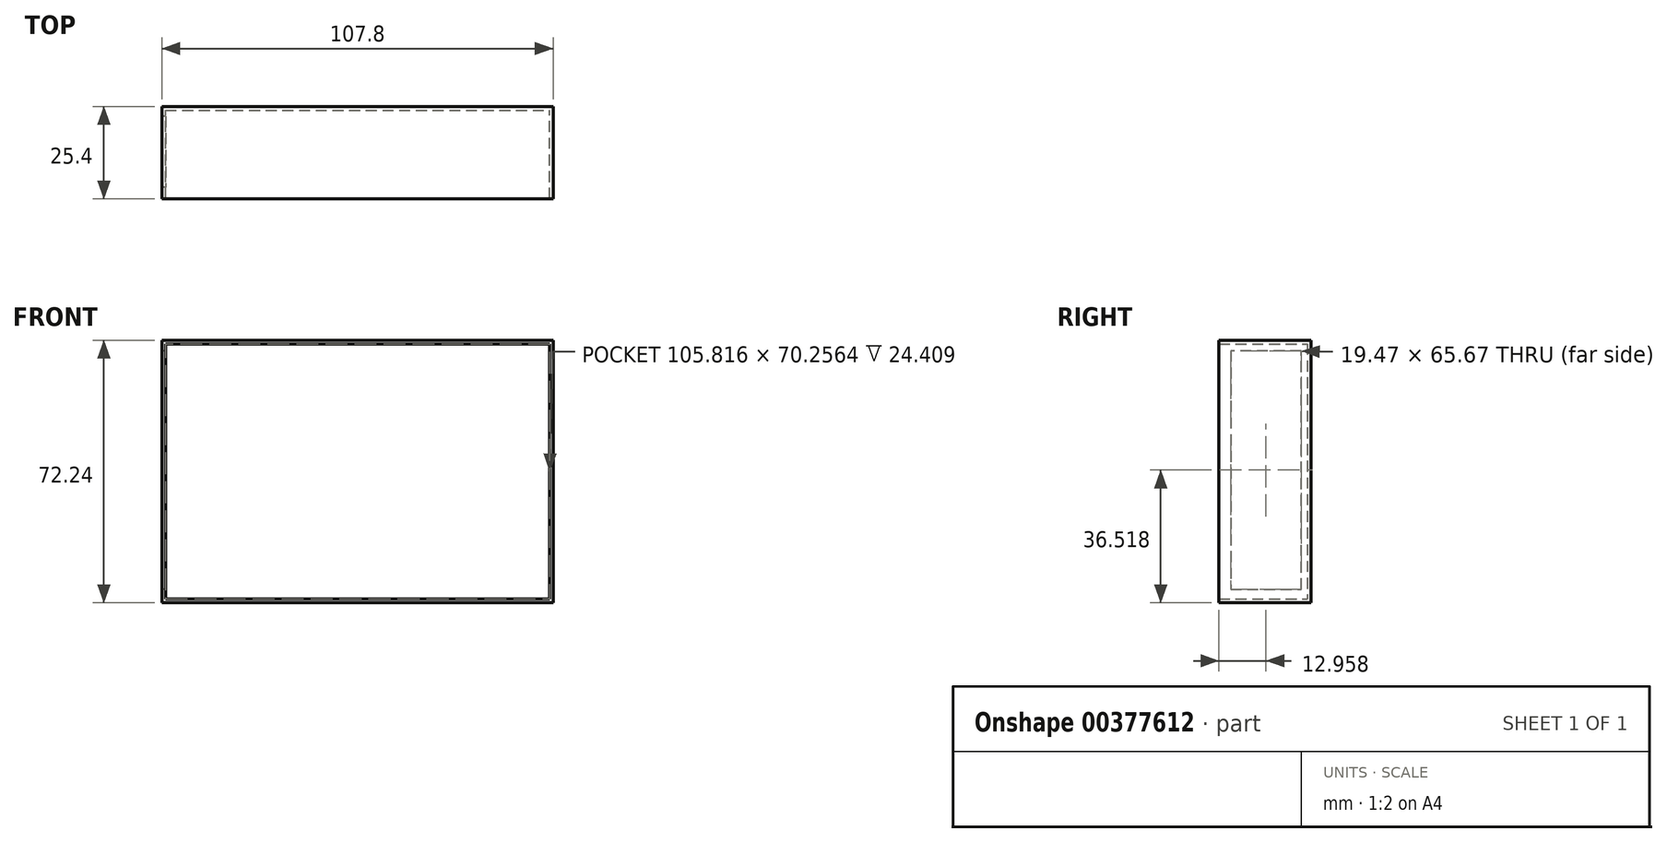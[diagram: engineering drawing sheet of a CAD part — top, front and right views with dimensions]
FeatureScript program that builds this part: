
annotation { "Feature Type Name" : "Feature", "Feature Type Description" : "" }
export const myFeature = defineFeature(function(context is Context, id is Id, definition is map)
    precondition{}
    {
        {
            var Q0;
            Q0=qCreatedBy(makeId("Front.planeOp"),FACE);
            var sketch = newSketch(context, id + "F0", { "sketchPlane" : qUnion([Q0])});
            skLineSegment(sketch, "E0.bottom", {"start": v(-53.9, 36.12) * mm, "end": v(53.9, 36.12) * mm});
            skLineSegment(sketch, "E0.top", {"start": v(-53.9, -36.12) * mm, "end": v(53.9, -36.12) * mm});
            skLineSegment(sketch, "E0.left", {"start": v(-53.9, 36.12) * mm, "end": v(-53.9, -36.12) * mm});
            skLineSegment(sketch, "E0.right", {"start": v(53.9, 36.12) * mm, "end": v(53.9, -36.12) * mm});
            skPoint(sketch, "E0.middle", {"position": v(0, 0) * mm});
            skSolve(sketch);
        }
        {
            var Q0;
            Q0 = qSketchRegion(id + "F0", true);
            extrude(context, id + "F1", {"entities" : qUnion([Q0]), "depth" : 25.4 * mm});
        }
        {
            var Q0;
            Q0=makeQuery(id+"F1.opExtrude","CAP_FACE",FACE,{"disambiguationData":[OSD([sQuery(id+"F0.wireOp",EDGE,"E0.bottom"),sQuery(id+"F0.wireOp",EDGE,"E0.top"),sQuery(id+"F0.wireOp",EDGE,"E0.left"),sQuery(id+"F0.wireOp",EDGE,"E0.right")])],"isStart":false});
            shell(context, id + "F2", {"entities" : qUnion([Q0]), "thickness" : 1 * mm});
        }
        {
            var Q0;
            Q0=makeQuery(id+"F1.opExtrude","SWEPT_FACE",FACE,{"disambiguationData":[OSD([sQuery(id+"F0.wireOp",EDGE,"E0.left")])]});
            var sketch = newSketch(context, id + "F3", { "sketchPlane" : qUnion([Q0])});
            skLineSegment(sketch, "E1", {"start": v(22.18, 33.23) * mm, "end": v(22.18, -32.44) * mm});
            skLineSegment(sketch, "E2", {"start": v(22.18, -32.44) * mm, "end": v(2.7, -32.44) * mm});
            skLineSegment(sketch, "E3", {"start": v(2.7, -32.44) * mm, "end": v(2.7, 33.23) * mm});
            skLineSegment(sketch, "E4", {"start": v(2.7, 33.23) * mm, "end": v(22.18, 33.23) * mm});
            skSolve(sketch);
        }
        {
            var Q0;
            Q0 = qSketchRegion(id + "F3", true);
            extrude(context, id + "F4", {"entities" : qUnion([Q0]), "operationType" : NewBodyOperationType.REMOVE, "oppositeDirection" : true, "depth" : 25.4 * mm});
        }
    });
